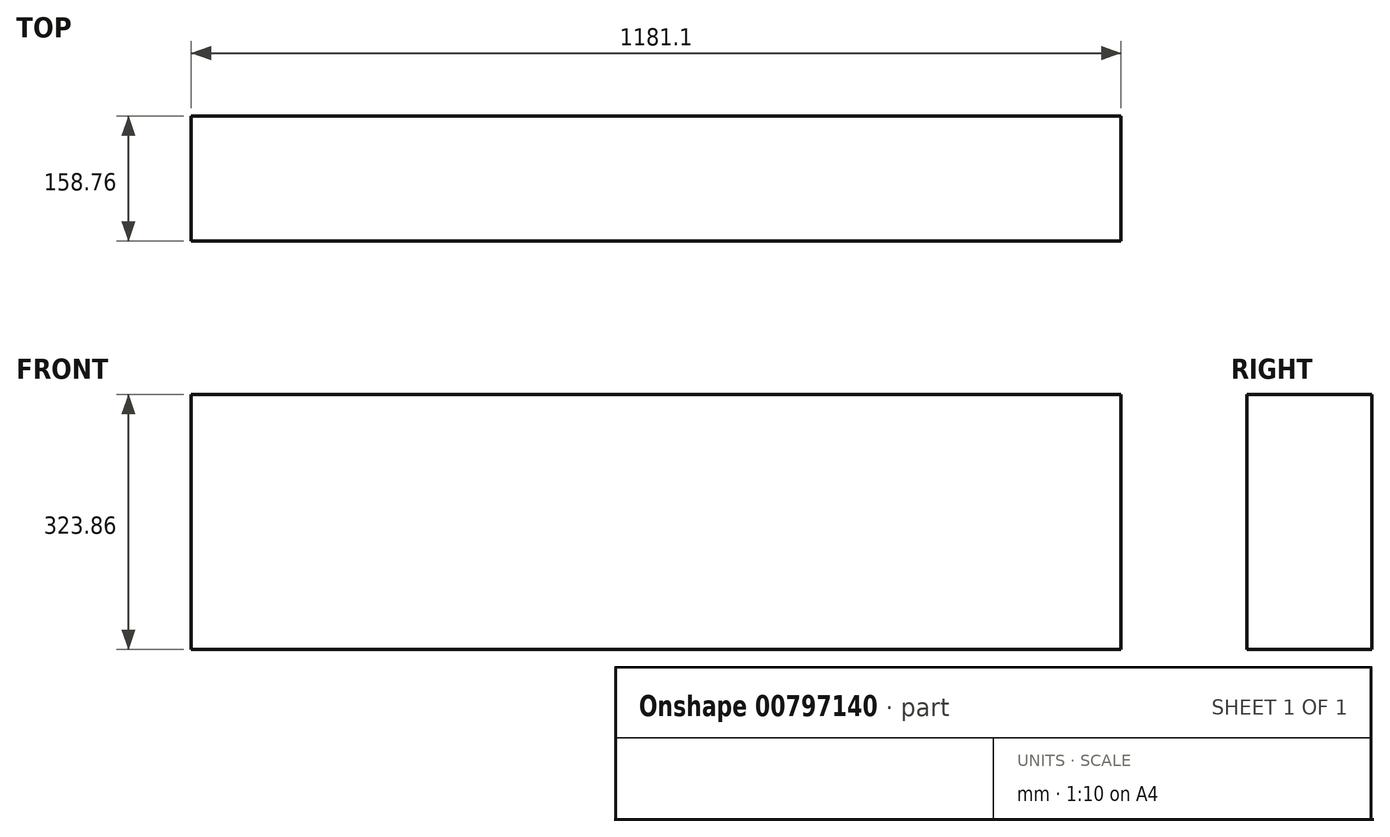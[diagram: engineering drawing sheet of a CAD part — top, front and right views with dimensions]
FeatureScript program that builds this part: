
annotation { "Feature Type Name" : "Feature", "Feature Type Description" : "" }
export const myFeature = defineFeature(function(context is Context, id is Id, definition is map)
    precondition{}
    {
        {
            var Q0;
            Q0=qCreatedBy(makeId("Front.planeOp"),FACE);
            var sketch = newSketch(context, id + "F0", { "sketchPlane" : qUnion([Q0])});
            skLineSegment(sketch, "E0.bottom", {"start": v(590.55, -161.93) * mm, "end": v(-590.55, -161.93) * mm});
            skLineSegment(sketch, "E0.top", {"start": v(590.55, 161.93) * mm, "end": v(-590.55, 161.92) * mm});
            skLineSegment(sketch, "E0.left", {"start": v(590.55, -161.93) * mm, "end": v(590.55, 161.93) * mm});
            skLineSegment(sketch, "E0.right", {"start": v(-590.55, -161.93) * mm, "end": v(-590.55, 161.92) * mm});
            skPoint(sketch, "E0.middle", {"position": v(0, 0) * mm});
            skSolve(sketch);
        }
        {
            var Q0;
            Q0=makeQuery(id+"F0.imprint","IMPRINT",FACE,{"disambiguationData":[TD([[makeQuery(id+"F0.imprint","IMPRINT",EDGE,{"derivedFrom":sQuery(id+"F0.wireOp",EDGE,"E0.bottom")}),-1.0]])]});
            extrude(context, id + "F1", {"entities" : qUnion([Q0]), "endBound" : BoundingType.SYMMETRIC, "depth" : 158.75 * mm, "offsetDistance" : 25.4 * mm});
        }
    });
